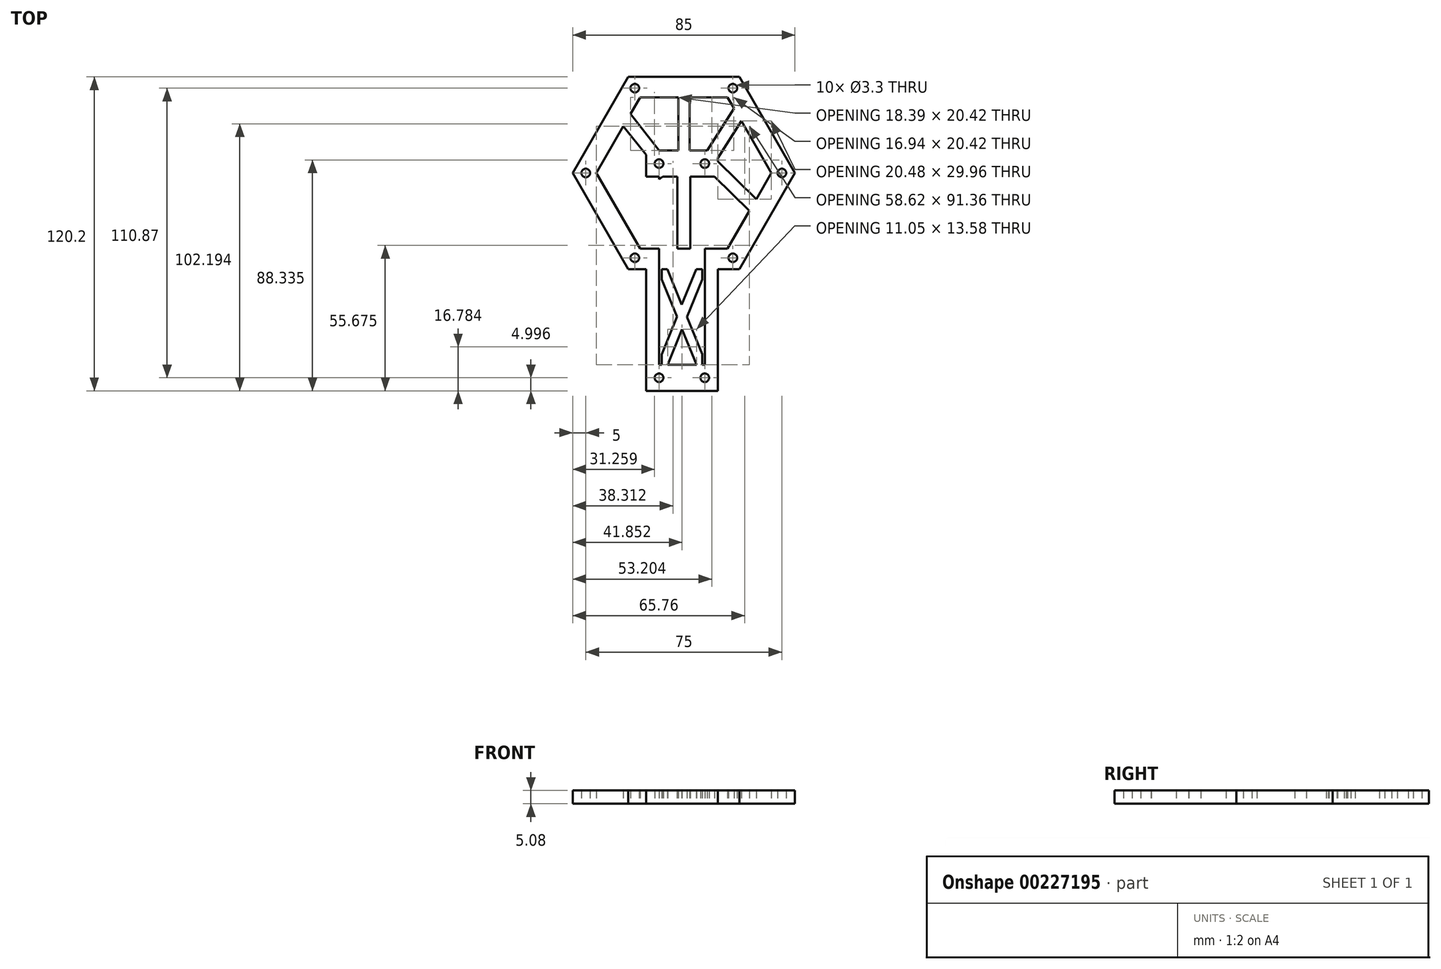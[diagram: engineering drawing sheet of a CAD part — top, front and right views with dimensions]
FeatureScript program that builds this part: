
annotation { "Feature Type Name" : "Feature", "Feature Type Description" : "" }
export const myFeature = defineFeature(function(context is Context, id is Id, definition is map)
    precondition{}
    {
        {
            var Q0;
            Q0=qCreatedBy(makeId("Top.planeOp"),FACE);
            var sketch = newSketch(context, id + "F0", { "sketchPlane" : qUnion([Q0])});
            skCircle(sketch, "E0.cCircle", {"center": v(0, 0) * mm, "radius": 32.48 * mm, "construction": true});
            skLineSegment(sketch, "E0.0", {"start": v(-18.75, 32.48) * mm, "end": v(18.75, 32.48) * mm, "construction": true});
            skLineSegment(sketch, "E0.1", {"start": v(18.75, 32.48) * mm, "end": v(37.5, 0) * mm, "construction": true});
            skLineSegment(sketch, "E0.2", {"start": v(37.5, 0) * mm, "end": v(18.75, -32.48) * mm, "construction": true});
            skLineSegment(sketch, "E0.3", {"start": v(18.75, -32.48) * mm, "end": v(-18.75, -32.48) * mm, "construction": true});
            skLineSegment(sketch, "E0.4", {"start": v(-18.75, -32.48) * mm, "end": v(-37.5, 0) * mm, "construction": true});
            skLineSegment(sketch, "E0.5", {"start": v(-37.5, 0) * mm, "end": v(-18.75, 32.48) * mm, "construction": true});
            skPoint(sketch, "E0.0.midPoint", {"position": v(0, 32.48) * mm});
            skCircle(sketch, "E1", {"center": v(-18.75, 32.48) * mm, "radius": 1.65 * mm});
            skCircle(sketch, "E2", {"center": v(18.75, 32.48) * mm, "radius": 1.65 * mm});
            skCircle(sketch, "E3", {"center": v(37.5, 0) * mm, "radius": 1.65 * mm});
            skCircle(sketch, "E4", {"center": v(18.75, -32.48) * mm, "radius": 1.65 * mm});
            skCircle(sketch, "E5", {"center": v(-18.75, -32.48) * mm, "radius": 1.65 * mm});
            skCircle(sketch, "E6", {"center": v(-37.5, 0) * mm, "radius": 1.65 * mm});
            skCircle(sketch, "E7.cCircle", {"center": v(0, 0) * mm, "radius": 36.8 * mm, "construction": true});
            skLineSegment(sketch, "E7.0", {"start": v(-21.25, 36.8) * mm, "end": v(21.25, 36.8) * mm});
            skLineSegment(sketch, "E7.1", {"start": v(21.25, 36.8) * mm, "end": v(42.5, 0) * mm});
            skLineSegment(sketch, "E7.2", {"start": v(42.5, 0) * mm, "end": v(21.25, -36.8) * mm});
            skLineSegment(sketch, "E7.3", {"start": v(21.25, -36.8) * mm, "end": v(-21.25, -36.8) * mm});
            skLineSegment(sketch, "E7.4", {"start": v(-21.25, -36.8) * mm, "end": v(-42.5, 0) * mm});
            skLineSegment(sketch, "E7.5", {"start": v(-42.5, 0) * mm, "end": v(-21.25, 36.8) * mm});
            skPoint(sketch, "E7.0.midPoint", {"position": v(0, 36.8) * mm});
            skCircle(sketch, "E8.cCircle", {"center": v(0, 0) * mm, "radius": 29.01 * mm, "construction": true});
            skLineSegment(sketch, "E8.0", {"start": v(-16.75, 29.01) * mm, "end": v(16.75, 29.01) * mm});
            skLineSegment(sketch, "E8.1", {"start": v(16.75, 29.01) * mm, "end": v(33.5, 0) * mm});
            skLineSegment(sketch, "E8.2", {"start": v(33.5, 0) * mm, "end": v(16.75, -29.01) * mm});
            skLineSegment(sketch, "E8.3", {"start": v(16.75, -29.01) * mm, "end": v(-16.75, -29.01) * mm});
            skLineSegment(sketch, "E8.4", {"start": v(-16.75, -29.01) * mm, "end": v(-33.5, 0) * mm});
            skLineSegment(sketch, "E8.5", {"start": v(-33.5, 0) * mm, "end": v(-16.75, 29.01) * mm});
            skPoint(sketch, "E8.0.midPoint", {"position": v(0, 29.01) * mm});
            skLineSegment(sketch, "E9", {"start": v(-9.48, 3.6) * mm, "end": v(8.02, 3.6) * mm, "construction": true});
            skLineSegment(sketch, "E10", {"start": v(-9.48, -78.4) * mm, "end": v(8.02, -78.4) * mm, "construction": true});
            skCircle(sketch, "E11", {"center": v(-9.48, 3.6) * mm, "radius": 1.65 * mm});
            skCircle(sketch, "E12", {"center": v(8.02, 3.6) * mm, "radius": 1.65 * mm});
            skCircle(sketch, "E13", {"center": v(-9.48, -78.4) * mm, "radius": 1.65 * mm});
            skCircle(sketch, "E14", {"center": v(8.02, -78.4) * mm, "radius": 1.65 * mm});
            skLineSegment(sketch, "E15.bottom", {"start": v(-14.48, 8.6) * mm, "end": v(13.02, 8.6) * mm});
            skLineSegment(sketch, "E15.top", {"start": v(-14.48, -1.4) * mm, "end": v(13.02, -1.4) * mm});
            skLineSegment(sketch, "E15.left", {"start": v(-14.48, 8.6) * mm, "end": v(-14.48, -1.4) * mm});
            skLineSegment(sketch, "E15.right", {"start": v(13.02, 8.6) * mm, "end": v(13.02, -1.4) * mm});
            skPoint(sketch, "E15.middle", {"position": v(-0.73, 3.6) * mm});
            skLineSegment(sketch, "E16.bottom", {"start": v(-14.48, -73.4) * mm, "end": v(13.02, -73.4) * mm});
            skLineSegment(sketch, "E16.top", {"start": v(-14.48, -83.4) * mm, "end": v(13.02, -83.4) * mm});
            skLineSegment(sketch, "E16.left", {"start": v(-14.48, -73.4) * mm, "end": v(-14.48, -83.4) * mm});
            skLineSegment(sketch, "E16.right", {"start": v(13.02, -73.4) * mm, "end": v(13.02, -83.4) * mm});
            skPoint(sketch, "E16.middle", {"position": v(-0.73, -78.4) * mm});
            skLineSegment(sketch, "E17", {"start": v(-14.48, -73.4) * mm, "end": v(-14.48, -36.8) * mm});
            skLineSegment(sketch, "E18", {"start": v(-8.48, -73.4) * mm, "end": v(-8.48, -36.8) * mm});
            skLineSegment(sketch, "E19", {"start": v(13.02, -73.4) * mm, "end": v(13.02, -36.8) * mm});
            skLineSegment(sketch, "E20", {"start": v(7.02, -73.4) * mm, "end": v(7.02, -36.8) * mm});
            skLineSegment(sketch, "E21", {"start": v(7.02, -55.1) * mm, "end": v(13.02, -55.1) * mm, "construction": true});
            skLineSegment(sketch, "E22", {"start": v(-14.48, -55.1) * mm, "end": v(-8.48, -55.1) * mm, "construction": true});
            skLineSegment(sketch, "E23", {"start": v(-6.34, -36.8) * mm, "end": v(7.02, -69.4) * mm});
            skLineSegment(sketch, "E24", {"start": v(7.02, -40.74) * mm, "end": v(-6.17, -73.4) * mm});
            skLineSegment(sketch, "E25", {"start": v(-8.48, -55.1) * mm, "end": v(7.02, -55.1) * mm, "construction": true});
            skLineSegment(sketch, "E26.1.0", {"start": v(4.88, -73.4) * mm, "end": v(-8.48, -40.8) * mm});
            skLineSegment(sketch, "E26.1.1", {"start": v(-8.48, -69.46) * mm, "end": v(4.71, -36.8) * mm});
            skPoint(sketch, "E26.center", {"position": v(-0.73, -55.1) * mm});
            skLineSegment(sketch, "E27", {"start": v(-9.4, 8.6) * mm, "end": v(-20.44, 22.63) * mm});
            skLineSegment(sketch, "E28", {"start": v(-14.48, 6.96) * mm, "end": v(-23.13, 17.96) * mm});
            skLineSegment(sketch, "E29", {"start": v(8.94, 8.6) * mm, "end": v(19.17, 24.82) * mm});
            skLineSegment(sketch, "E30", {"start": v(13.02, 5.68) * mm, "end": v(22, 19.92) * mm});
            skLineSegment(sketch, "E31", {"start": v(13.02, 4.39) * mm, "end": v(27.7, -10.03) * mm});
            skLineSegment(sketch, "E32", {"start": v(11.78, -1.4) * mm, "end": v(25.13, -14.5) * mm});
            skLineSegment(sketch, "E33", {"start": v(-8.1, -1.4) * mm, "end": v(-25.12, -14.5) * mm});
            skLineSegment(sketch, "E34", {"start": v(-14.48, 0) * mm, "end": v(-27.65, -10.14) * mm});
            skLineSegment(sketch, "E35", {"start": v(-20.15, -4.36) * mm, "end": v(-17.1, -8.33) * mm, "construction": true});
            skLineSegment(sketch, "E36", {"start": v(16.32, -5.86) * mm, "end": v(19.83, -2.3) * mm, "construction": true});
            skLineSegment(sketch, "E37", {"start": v(16.82, 11.7) * mm, "end": v(12.59, 14.38) * mm, "construction": true});
            skLineSegment(sketch, "E38", {"start": v(-18.2, 11.7) * mm, "end": v(-14.27, 14.79) * mm, "construction": true});
            skLineSegment(sketch, "E39", {"start": v(-2.5, -1.4) * mm, "end": v(-2.5, -29.01) * mm});
            skLineSegment(sketch, "E40", {"start": v(2.5, -1.4) * mm, "end": v(2.5, -29.01) * mm});
            skLineSegment(sketch, "E41", {"start": v(-2.5, -10.42) * mm, "end": v(2.5, -10.42) * mm, "construction": true});
            skLineSegment(sketch, "E42", {"start": v(-2.05, 8.6) * mm, "end": v(-2.05, 29.01) * mm});
            skLineSegment(sketch, "E43", {"start": v(2.24, 8.6) * mm, "end": v(2.24, 29.01) * mm});
            skLineSegment(sketch, "E44", {"start": v(-2.05, 18.8) * mm, "end": v(2.24, 18.8) * mm, "construction": true});
            skLineSegment(sketch, "E45", {"start": v(-9.48, 3.6) * mm, "end": v(-9.48, -78.4) * mm});
            skLineSegment(sketch, "E46", {"start": v(8.02, -78.4) * mm, "end": v(8.02, 3.6) * mm});
            skSolve(sketch);
        }
        {
            var Q0;
            Q0=makeQuery(id+"F0.imprint","IMPRINT",FACE,{"disambiguationData":[TD([[makeQuery(id+"F0.imprint","IMPRINT",EDGE,{"derivedFrom":sQuery(id+"F0.wireOp",EDGE,"E1")}),-1.0]])]});
            var Q1;
            {var subQ4=sQuery(id+"F0.wireOp",EDGE,"9ny764Z0-yEnc-nTom-sgEr-T5m8jRU7CaOd");Q1=makeQuery(id+"F0.imprint","IMPRINT",FACE,{"disambiguationData":[TD([[makeQuery(id+"F0.imprint","IMPRINT",EDGE,{"derivedFrom":subQ4}),1.0]])]});}
            var Q2;
            {var subQ0=sQuery(id+"F0.wireOp",EDGE,"mveJp2gq-viMz-v7hY-WbP1-sUx4nALb4Kya");Q2=makeQuery(id+"F0.imprint","IMPRINT",FACE,{"disambiguationData":[TD([[makeQuery(id+"F0.imprint","IMPRINT",EDGE,{"derivedFrom":subQ0}),-1.0]])]});}
            var Q3;
            {var subQ0=sQuery(id+"F0.wireOp",EDGE,"Fl41E3Zq-ps3j-7aEv-HD6p-v4TBVcw58FQC");Q3=makeQuery(id+"F0.imprint","IMPRINT",FACE,{"disambiguationData":[TD([[makeQuery(id+"F0.imprint","IMPRINT",EDGE,{"derivedFrom":subQ0}),1.0]])]});}
            var Q4;
            Q4=makeQuery(id+"F0.imprint","IMPRINT",FACE,{"disambiguationData":[TD([[makeQuery(id+"F0.imprint","IMPRINT",EDGE,{"derivedFrom":sQuery(id+"F0.wireOp",EDGE,"E11")}),-1.0]])]});
            var Q5;
            {var subQ0=sQuery(id+"F0.wireOp",EDGE,"ZUoPdMyJ-yNmC-lj2F-qgpw-CtUOoCRU5N7t");Q5=makeQuery(id+"F0.imprint","IMPRINT",FACE,{"disambiguationData":[TD([[makeQuery(id+"F0.imprint","IMPRINT",EDGE,{"derivedFrom":subQ0}),1.0]])]});}
            var Q6;
            {var subQ4=sQuery(id+"F0.wireOp",EDGE,"E17");Q6=makeQuery(id+"F0.imprint","IMPRINT",FACE,{"disambiguationData":[TD([[makeQuery(id+"F0.imprint","IMPRINT",EDGE,{"derivedFrom":subQ4}),-1.0]])]});}
            var Q7;
            {var subQ4=sQuery(id+"F0.wireOp",EDGE,"E19");Q7=makeQuery(id+"F0.imprint","IMPRINT",FACE,{"disambiguationData":[TD([[makeQuery(id+"F0.imprint","IMPRINT",EDGE,{"derivedFrom":subQ4}),1.0]])]});}
            var Q8;
            {var subQ1=sQuery(id+"F0.wireOp",EDGE,"E20");var subQ7=sQuery(id+"F0.wireOp",EDGE,"E7.3");var subQ8=makeQuery(id+"F0.imprint","INTERSECT",VERTEX,{"derivedFrom":[subQ7,subQ1]});Q8=makeQuery(id+"F0.imprint","IMPRINT",FACE,{"disambiguationData":[TD([[makeQuery(id+"F0.imprint","IMPRINT",EDGE,{"disambiguationData":[TD([[subQ8,-1.0]])],"derivedFrom":subQ7}),1.0]])]});}
            var Q9;
            {var subQ1=sQuery(id+"F0.wireOp",EDGE,"E18");var subQ6=sQuery(id+"F0.wireOp",EDGE,"E7.3");var subQ9=makeQuery(id+"F0.imprint","INTERSECT",VERTEX,{"derivedFrom":[subQ6,subQ1]});Q9=makeQuery(id+"F0.imprint","IMPRINT",FACE,{"disambiguationData":[TD([[makeQuery(id+"F0.imprint","IMPRINT",EDGE,{"disambiguationData":[TD([[subQ9,1.0]])],"derivedFrom":subQ6}),1.0]])]});}
            var Q10;
            {var subQ0=sQuery(id+"F0.wireOp",EDGE,"E26.1.1");var subQ1=sQuery(id+"F0.wireOp",EDGE,"E23");var subQ2=makeQuery(id+"F0.imprint","INTERSECT",VERTEX,{"derivedFrom":[subQ1,subQ0]});Q10=makeQuery(id+"F0.imprint","IMPRINT",FACE,{"disambiguationData":[TD([[makeQuery(id+"F0.imprint","IMPRINT",EDGE,{"disambiguationData":[TD([[subQ2,-1.0]])],"derivedFrom":subQ1}),-1.0]])]});}
            var Q11;
            {var subQ5=sQuery(id+"F0.wireOp",EDGE,"E18");var subQ6=sQuery(id+"F0.wireOp",EDGE,"E16.bottom");var subQ7=makeQuery(id+"F0.imprint","INTERSECT",VERTEX,{"derivedFrom":[subQ6,subQ5]});Q11=makeQuery(id+"F0.imprint","IMPRINT",FACE,{"disambiguationData":[TD([[makeQuery(id+"F0.imprint","IMPRINT",EDGE,{"disambiguationData":[TD([[subQ7,-1.0]])],"derivedFrom":subQ6}),1.0]])]});}
            var Q12;
            {var subQ5=sQuery(id+"F0.wireOp",EDGE,"E20");var subQ7=sQuery(id+"F0.wireOp",EDGE,"E16.bottom");var subQ8=makeQuery(id+"F0.imprint","INTERSECT",VERTEX,{"derivedFrom":[subQ7,subQ5]});Q12=makeQuery(id+"F0.imprint","IMPRINT",FACE,{"disambiguationData":[TD([[makeQuery(id+"F0.imprint","IMPRINT",EDGE,{"disambiguationData":[TD([[subQ8,1.0]])],"derivedFrom":subQ7}),1.0]])]});}
            var Q13;
            Q13=makeQuery(id+"F0.imprint","IMPRINT",FACE,{"disambiguationData":[TD([[makeQuery(id+"F0.imprint","IMPRINT",EDGE,{"derivedFrom":sQuery(id+"F0.wireOp",EDGE,"E13")}),-1.0]])]});
            var Q14;
            {var subQ4=sQuery(id+"F0.wireOp",EDGE,"E27");Q14=makeQuery(id+"F0.imprint","IMPRINT",FACE,{"disambiguationData":[TD([[makeQuery(id+"F0.imprint","IMPRINT",EDGE,{"derivedFrom":subQ4}),1.0]])]});}
            var Q15;
            {var subQ0=sQuery(id+"F0.wireOp",EDGE,"E42");Q15=makeQuery(id+"F0.imprint","IMPRINT",FACE,{"disambiguationData":[TD([[makeQuery(id+"F0.imprint","IMPRINT",EDGE,{"derivedFrom":subQ0}),-1.0]])]});}
            var Q16;
            {var subQ0=sQuery(id+"F0.wireOp",EDGE,"E29");Q16=makeQuery(id+"F0.imprint","IMPRINT",FACE,{"disambiguationData":[TD([[makeQuery(id+"F0.imprint","IMPRINT",EDGE,{"derivedFrom":subQ0}),-1.0]])]});}
            var Q17;
            {var subQ0=sQuery(id+"F0.wireOp",EDGE,"E31");Q17=makeQuery(id+"F0.imprint","IMPRINT",FACE,{"disambiguationData":[TD([[makeQuery(id+"F0.imprint","IMPRINT",EDGE,{"derivedFrom":subQ0}),-1.0]])]});}
            var Q18;
            {var subQ4=sQuery(id+"F0.wireOp",EDGE,"E33");Q18=makeQuery(id+"F0.imprint","IMPRINT",FACE,{"disambiguationData":[TD([[makeQuery(id+"F0.imprint","IMPRINT",EDGE,{"derivedFrom":subQ4}),-1.0]])]});}
            var Q19;
            {var subQ0=sQuery(id+"F0.wireOp",EDGE,"E39");Q19=makeQuery(id+"F0.imprint","IMPRINT",FACE,{"disambiguationData":[TD([[makeQuery(id+"F0.imprint","IMPRINT",EDGE,{"derivedFrom":subQ0}),1.0]])]});}
            extrude(context, id + "F1", {"entities" : qUnion([Q0, Q1, Q2, Q3, Q4, Q5, Q6, Q7, Q8, Q9, Q10, Q11, Q12, Q13, Q14, Q15, Q16, Q17, Q18, Q19]), "depth" : 5.08 * mm});
        }
    });
